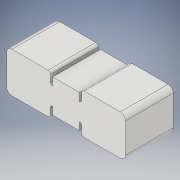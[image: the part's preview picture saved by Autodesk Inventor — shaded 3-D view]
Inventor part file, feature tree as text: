
AUTODESK INVENTOR PART (.ipt)
format: ipt  version: 2017 (Build 210142000, 142)  size: 136,192 bytes
history: native  units: in
note: dims shown in document units (in); Inventor stores cm internally (conversion verified against a paired STEP export)
features: extrude x1, sketch x1
ambient origin geometry x8: Origin, YZ Plane, XZ Plane, XY Plane, X Axis, Y Axis, Z Axis, Center Point
bodies: Solid1 (feature_tree)
feature tree (2):
  extrude  "Extrusion1"  Depth=0.85in
  sketch  "Sketch1"  dims[d1=0.39in d2=0.85in d3=0.22in d4=0.04in d5=0.32in d6=0.1in d7=0.05in d8=0.04in d9=0.926in d10=0.0in]
